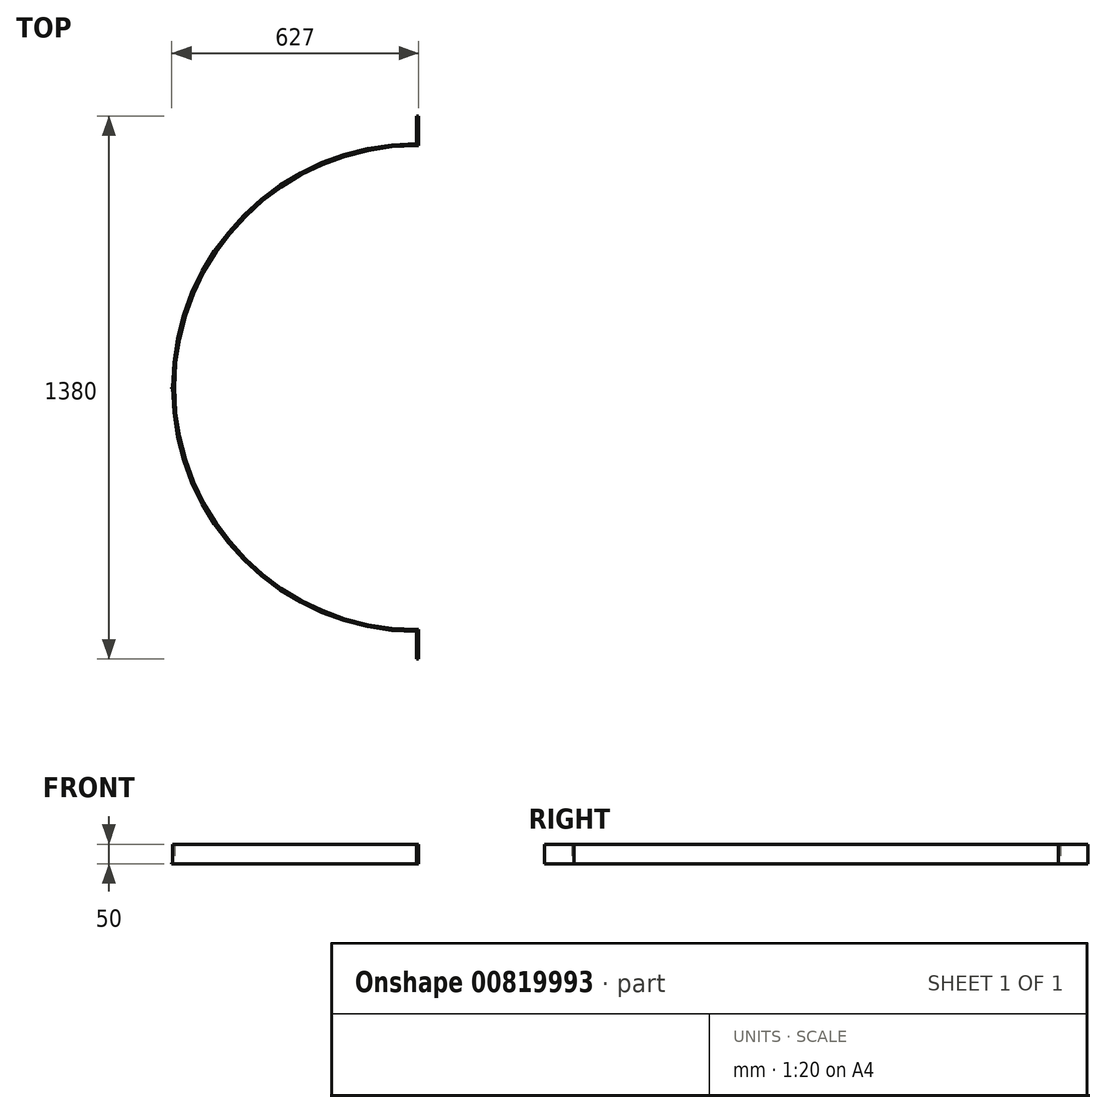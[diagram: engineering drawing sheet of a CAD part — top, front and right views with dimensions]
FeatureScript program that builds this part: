
annotation { "Feature Type Name" : "Feature", "Feature Type Description" : "" }
export const myFeature = defineFeature(function(context is Context, id is Id, definition is map)
    precondition{}
    {
        {
            var Q0;
            Q0=qCreatedBy(makeId("Top.planeOp"),FACE);
            var sketch = newSketch(context, id + "F0", { "sketchPlane" : qUnion([Q0])});
            skArc(sketch, "E0", {"start": v(-620, 0) * mm, "mid": v(-438.4, -438.4) * mm, "end": v(0, -620) * mm});
            skLineSegment(sketch, "E1", {"start": v(0, 0) * mm, "end": v(0, -620) * mm, "construction": true});
            skLineSegment(sketch, "E2", {"start": v(0, 0) * mm, "end": v(-620, 0) * mm, "construction": true});
            skArc(sketch, "E3.0", {"start": v(-615, 0) * mm, "mid": v(-434.87, -434.87) * mm, "end": v(0, -615) * mm});
            skLineSegment(sketch, "E4", {"start": v(0, -615) * mm, "end": v(0, -690) * mm});
            skLineSegment(sketch, "E5", {"start": v(0, -690) * mm, "end": v(5, -690) * mm});
            skLineSegment(sketch, "E6", {"start": v(5, -690) * mm, "end": v(5, -615) * mm});
            skLineSegment(sketch, "E7", {"start": v(5, -615) * mm, "end": v(0, -615) * mm});
            skLineSegment(sketch, "E8", {"start": v(-615, 0) * mm, "end": v(-620, 0) * mm});
            skSolve(sketch);
        }
        {
            var Q0;
            Q0=qSketchRegion(id+"F0",true);
            extrude(context, id + "F1", {"entities" : qUnion([Q0]), "depth" : 50 * mm, "offsetDistance" : 25 * mm});
        }
        {
            var Q0;
            Q0=makeQuery(id+"F1.opExtrude","SWEPT_BODY",BODY,{"disambiguationData":[OSD([sQuery(id+"F0.wireOp",EDGE,"E0"),sQuery(id+"F0.wireOp",EDGE,"E3.0"),sQuery(id+"F0.wireOp",EDGE,"E4"),sQuery(id+"F0.wireOp",EDGE,"E5"),sQuery(id+"F0.wireOp",EDGE,"E6"),sQuery(id+"F0.wireOp",EDGE,"E7"),sQuery(id+"F0.wireOp",EDGE,"E8")])]});
            var Q1;
            Q1=makeQuery(id+"F1.opExtrude","SWEPT_FACE",FACE,{"disambiguationData":[OSD([sQuery(id+"F0.wireOp",EDGE,"E8")])]});
            mirror(context, id + "F2", {"operationType" : NewBodyOperationType.ADD, "entities" : qUnion([Q0]), "mirrorPlane" : qUnion([Q1])});
        }
        {
            var Q0;
            Q0=qCreatedBy(makeId("Front.planeOp"),FACE);
            var sketch = newSketch(context, id + "F3", { "sketchPlane" : qUnion([Q0])});
            skLineSegment(sketch, "E9", {"start": v(0, 0) * mm, "end": v(-620, 0) * mm});
            skLineSegment(sketch, "E10", {"start": v(-620, 0) * mm, "end": v(-622, 0) * mm});
            skLineSegment(sketch, "E11", {"start": v(-622, 0) * mm, "end": v(-622, 2) * mm});
            skLineSegment(sketch, "E12", {"start": v(-622, 2) * mm, "end": v(-620, 2) * mm});
            skLineSegment(sketch, "E13", {"start": v(-620, 2) * mm, "end": v(-620, 0) * mm});
            skSolve(sketch);
        }
        {
            var Q0;
            Q0=qSketchRegion(id+"F3",true);
            extrude(context, id + "F4", {"entities" : qUnion([Q0]), "depth" : 2 * mm, "offsetDistance" : 25 * mm});
        }
    });
